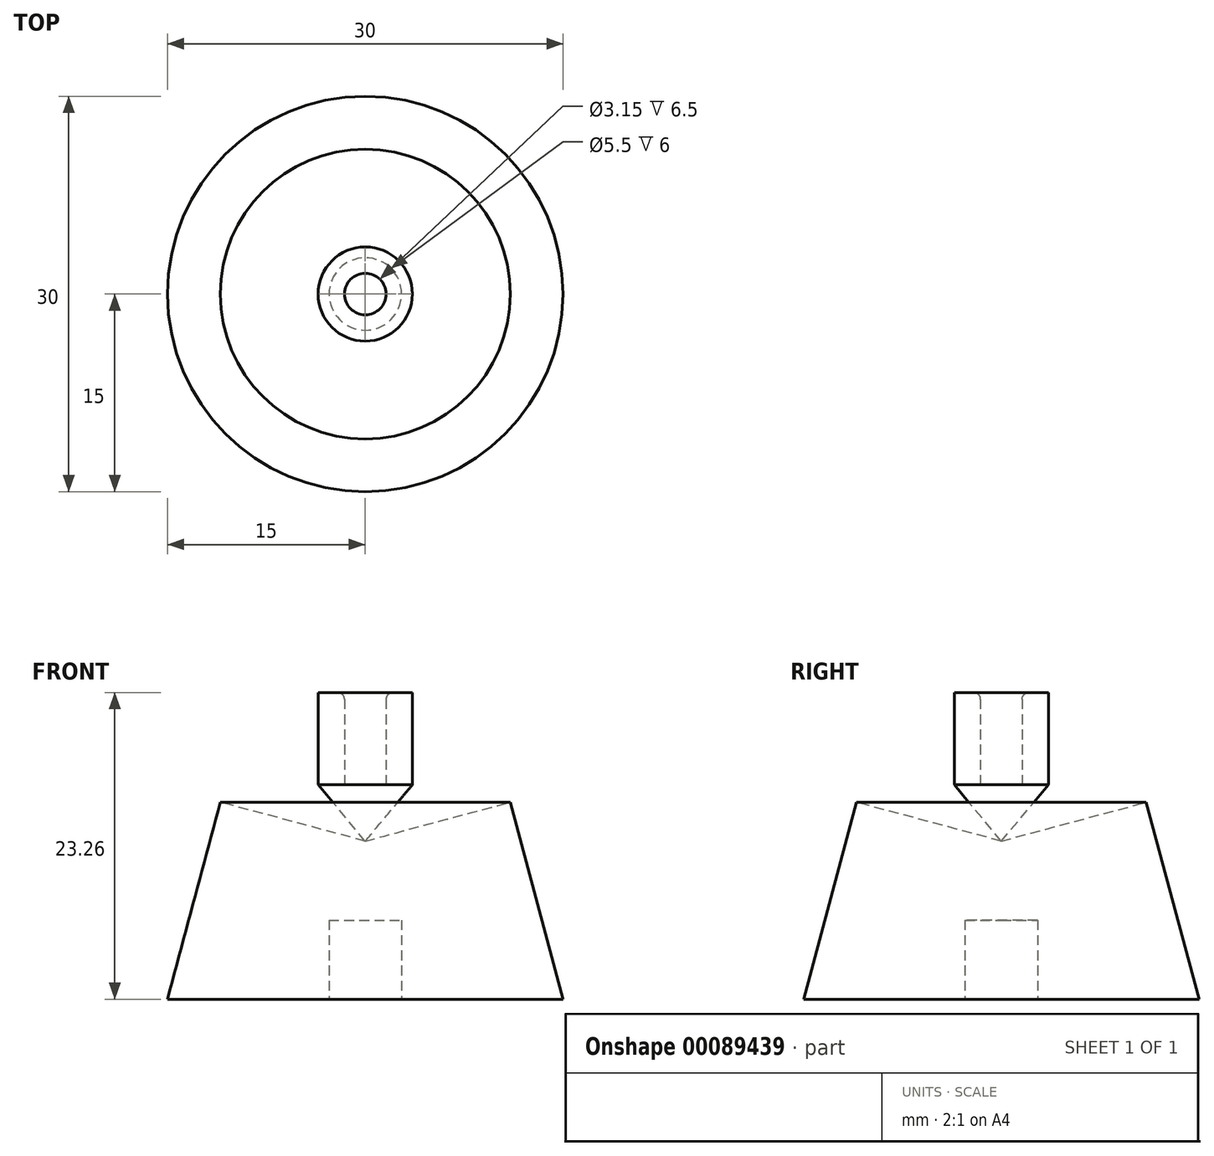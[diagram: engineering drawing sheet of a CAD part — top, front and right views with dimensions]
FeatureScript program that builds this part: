
annotation { "Feature Type Name" : "Feature", "Feature Type Description" : "" }
export const myFeature = defineFeature(function(context is Context, id is Id, definition is map)
    precondition{}
    {
        {
            var Q0;
            Q0=qCreatedBy(makeId("Front.planeOp"),FACE);
            var sketch = newSketch(context, id + "F0", { "sketchPlane" : qUnion([Q0])});
            skLineSegment(sketch, "E0", {"start": v(0, 0) * mm, "end": v(0, 4.38) * mm, "construction": true});
            skLineSegment(sketch, "E1", {"start": v(0, -4.26) * mm, "end": v(3.58, 0) * mm});
            skLineSegment(sketch, "E2", {"start": v(3.58, 0) * mm, "end": v(3.58, 7) * mm});
            skLineSegment(sketch, "E3", {"start": v(3.58, 7) * mm, "end": v(1.57, 7) * mm});
            skLineSegment(sketch, "E4", {"start": v(1.57, 7) * mm, "end": v(1.57, 0) * mm});
            skLineSegment(sketch, "E5", {"start": v(1.57, 0) * mm, "end": v(0, 0) * mm});
            skLineSegment(sketch, "E6", {"start": v(0, -4.26) * mm, "end": v(0, 0) * mm});
            skLineSegment(sketch, "E7", {"start": v(11, -1.31) * mm, "end": v(0, -4.26) * mm});
            skLineSegment(sketch, "E8", {"start": v(15, -16.26) * mm, "end": v(11, -1.31) * mm});
            skLineSegment(sketch, "E9", {"start": v(15, -16.26) * mm, "end": v(0, -16.26) * mm});
            skLineSegment(sketch, "E10", {"start": v(0, -16.26) * mm, "end": v(0, -4.26) * mm});
            skLineSegment(sketch, "E11", {"start": v(2.75, -16.26) * mm, "end": v(2.75, -10.26) * mm});
            skLineSegment(sketch, "E12", {"start": v(2.75, -10.26) * mm, "end": v(0, -10.26) * mm});
            skSolve(sketch);
        }
        {
            var Q0;
            {var subQ1=sQuery(id+"F0.wireOp",EDGE,"E7");Q0=makeQuery(id+"F0.imprint","IMPRINT",FACE,{"disambiguationData":[TD([[makeQuery(id+"F0.imprint","IMPRINT",EDGE,{"derivedFrom":subQ1}),1.0]])]});}
            var Q1;
            Q1=makeQuery(id+"F0.imprint","IMPRINT",FACE,{"disambiguationData":[TD([[makeQuery(id+"F0.imprint","IMPRINT",EDGE,{"derivedFrom":sQuery(id+"F0.wireOp",EDGE,"E1")}),1.0]])]});
            var Q2;
            Q2=sQuery(id+"F0.wireOp",EDGE,"E0");
            revolve(context, id + "F1", {"entities" : qUnion([Q0, Q1]), "axis" : qUnion([Q2]), "revolveType" : RevolveType.FULL});
        }
        {
            var Q0;
            Q0=makeQuery(id+"F1.opRevolve","SWEPT_EDGE",EDGE,{"disambiguationData":[OSD([sQuery(id+"F0.wireOp",EDGE,"E3"),sQuery(id+"F0.wireOp",EDGE,"E4")])]});
            fillet(context, id + "F2", {"entities" : qUnion([Q0]), "radius" : 0.5 * mm, "tangentPropagation" : true, "allowEdgeOverflow" : false});
        }
    });
